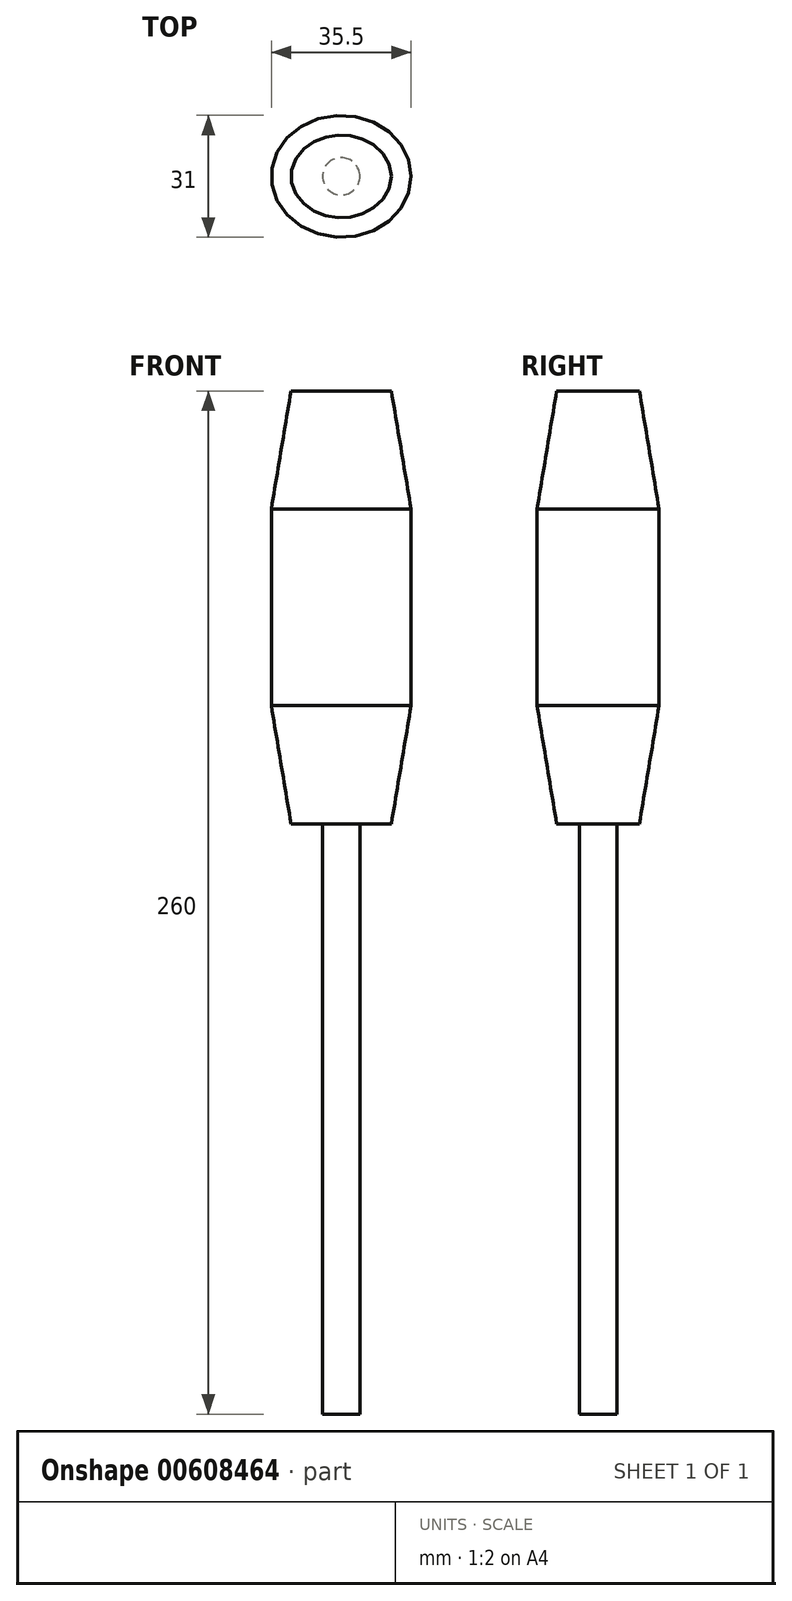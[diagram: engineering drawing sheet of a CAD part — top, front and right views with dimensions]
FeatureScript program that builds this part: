
annotation { "Feature Type Name" : "Feature", "Feature Type Description" : "" }
export const myFeature = defineFeature(function(context is Context, id is Id, definition is map)
    precondition{}
    {
        {
            var Q0;
            Q0=qCreatedBy(makeId("Top.planeOp"),FACE);
            var sketch = newSketch(context, id + "F0", { "sketchPlane" : qUnion([Q0])});
            skEllipse(sketch, "E0", {"center": v(0, 0) * mm, "majorRadius": 17.75 * mm, "minorRadius": 15.5 * mm, "majorAxis": v(1, 0)});
            skSolve(sketch);
        }
        {
            var Q0;
            Q0=makeQuery(id+"F0.imprint","IMPRINT",FACE,{"disambiguationData":[TD([[makeQuery(id+"F0.imprint","IMPRINT",EDGE,{"derivedFrom":sQuery(id+"F0.wireOp",EDGE,"E0")}),1.0]])]});
            extrude(context, id + "F1", {"entities" : qUnion([Q0]), "depth" : 110 * mm, "offsetDistance" : 25 * mm});
        }
        {
            var Q0;
            Q0=makeQuery(id+"F1.opExtrude","CAP_FACE",FACE,{"disambiguationData":[OSD([sQuery(id+"F0.wireOp",EDGE,"E0")])],"isStart":true});
            var sketch = newSketch(context, id + "F2", { "sketchPlane" : qUnion([Q0])});
            skCircle(sketch, "E1", {"center": v(0, 0) * mm, "radius": 4.75 * mm});
            skSolve(sketch);
        }
        {
            var Q0;
            Q0=qSketchRegion(id+"F2",true);
            extrude(context, id + "F3", {"entities" : qUnion([Q0]), "operationType" : NewBodyOperationType.ADD, "depth" : 150 * mm, "offsetDistance" : 25 * mm});
        }
        {
            var Q0;
            Q0=makeQuery(id+"F1.opExtrude","CAP_EDGE",EDGE,{"disambiguationData":[OSD([sQuery(id+"F0.wireOp",EDGE,"E0")])],"isStart":false});
            var Q1;
            Q1=makeQuery(id+"F1.opExtrude","CAP_EDGE",EDGE,{"disambiguationData":[OSD([sQuery(id+"F0.wireOp",EDGE,"E0")])],"isStart":true});
            chamfer(context, id + "F4", {"entities" : qUnion([Q0, Q1]), "chamferType" : ChamferType.TWO_OFFSETS, "width1" : 5 * mm, "oppositeDirection" : false, "width2" : 30 * mm, "tangentPropagation" : true});
        }
    });
